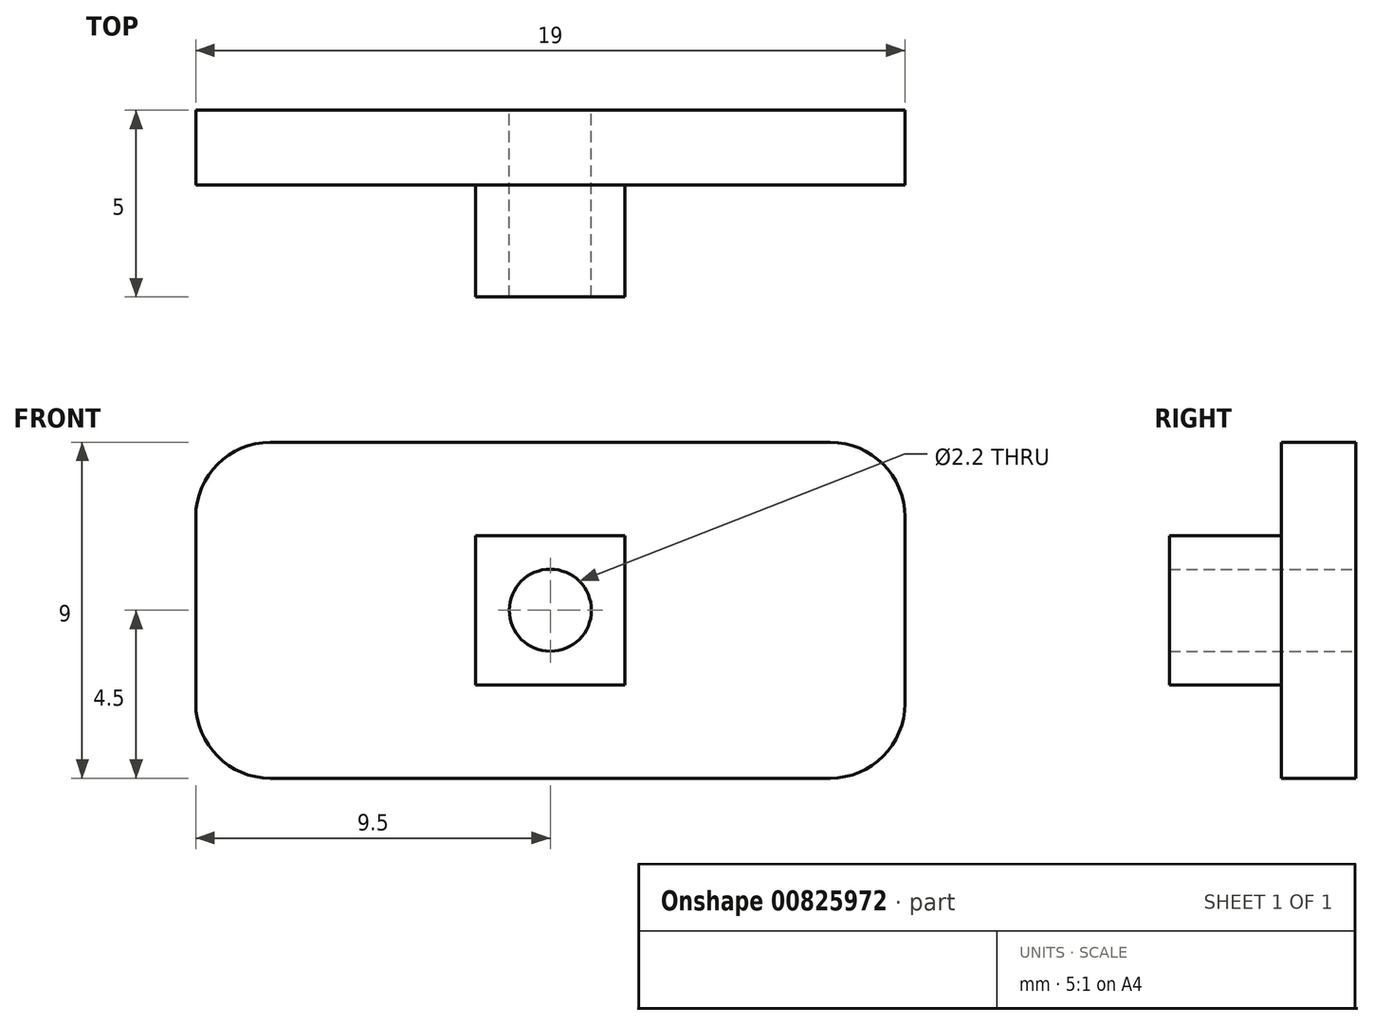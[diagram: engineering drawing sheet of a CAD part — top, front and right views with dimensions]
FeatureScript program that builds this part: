
annotation { "Feature Type Name" : "Feature", "Feature Type Description" : "" }
export const myFeature = defineFeature(function(context is Context, id is Id, definition is map)
    precondition{}
    {
        {
            var Q0;
            Q0=qCreatedBy(makeId("Front.planeOp"),FACE);
            var sketch = newSketch(context, id + "F0", { "sketchPlane" : qUnion([Q0])});
            skLineSegment(sketch, "E0.bottom", {"start": v(7.5, -4.5) * mm, "end": v(-7.5, -4.5) * mm});
            skLineSegment(sketch, "E0.top", {"start": v(7.5, 4.5) * mm, "end": v(-7.5, 4.5) * mm});
            skLineSegment(sketch, "E0.left", {"start": v(9.5, -2.5) * mm, "end": v(9.5, 2.5) * mm});
            skLineSegment(sketch, "E0.right", {"start": v(-9.5, -2.5) * mm, "end": v(-9.5, 2.5) * mm});
            skPoint(sketch, "E0.middle", {"position": v(0, 0) * mm});
            skPoint(sketch, "E1.visualSharp", {"position": v(-9.5, 4.5) * mm});
            skArc(sketch, "E1.filletArc", {"start": v(-7.5, 4.5) * mm, "mid": v(-8.91, 3.91) * mm, "end": v(-9.5, 2.5) * mm});
            skPoint(sketch, "E2.visualSharp", {"position": v(9.5, 4.5) * mm});
            skArc(sketch, "E2.filletArc", {"start": v(9.5, 2.5) * mm, "mid": v(8.91, 3.91) * mm, "end": v(7.5, 4.5) * mm});
            skPoint(sketch, "E3.visualSharp", {"position": v(9.5, -4.5) * mm});
            skArc(sketch, "E3.filletArc", {"start": v(7.5, -4.5) * mm, "mid": v(8.91, -3.91) * mm, "end": v(9.5, -2.5) * mm});
            skPoint(sketch, "E4.visualSharp", {"position": v(-9.5, -4.5) * mm});
            skArc(sketch, "E4.filletArc", {"start": v(-9.5, -2.5) * mm, "mid": v(-8.91, -3.91) * mm, "end": v(-7.5, -4.5) * mm});
            skLineSegment(sketch, "E5.bottom", {"start": v(2, -2) * mm, "end": v(-2, -2) * mm});
            skLineSegment(sketch, "E5.top", {"start": v(2, 2) * mm, "end": v(-2, 2) * mm});
            skLineSegment(sketch, "E5.left", {"start": v(2, -2) * mm, "end": v(2, 2) * mm});
            skLineSegment(sketch, "E5.right", {"start": v(-2, -2) * mm, "end": v(-2, 2) * mm});
            skCircle(sketch, "E6", {"center": v(0, 0) * mm, "radius": 1.1 * mm});
            skSolve(sketch);
        }
        {
            var Q0;
            Q0 = qSketchRegion(id + "F0", true);
            var Q1;
            Q1=makeQuery(id+"F0.imprint","IMPRINT",FACE,{"disambiguationData":[TD([[makeQuery(id+"F0.imprint","IMPRINT",EDGE,{"derivedFrom":sQuery(id+"F0.wireOp",EDGE,"E0.bottom")}),-1.0]])]});
            extrude(context, id + "F1", {"entities" : qUnion([Q0, Q1]), "depth" : 2 * mm, "offsetDistance" : 25 * mm});
        }
        {
            var Q0;
            Q0=makeQuery(id+"F0.imprint","IMPRINT",FACE,{"disambiguationData":[TD([[makeQuery(id+"F0.imprint","IMPRINT",EDGE,{"derivedFrom":sQuery(id+"F0.wireOp",EDGE,"E5.bottom")}),-1.0]])]});
            extrude(context, id + "F2", {"entities" : qUnion([Q0]), "operationType" : NewBodyOperationType.ADD, "depth" : 5 * mm, "offsetDistance" : 25 * mm});
        }
    });
